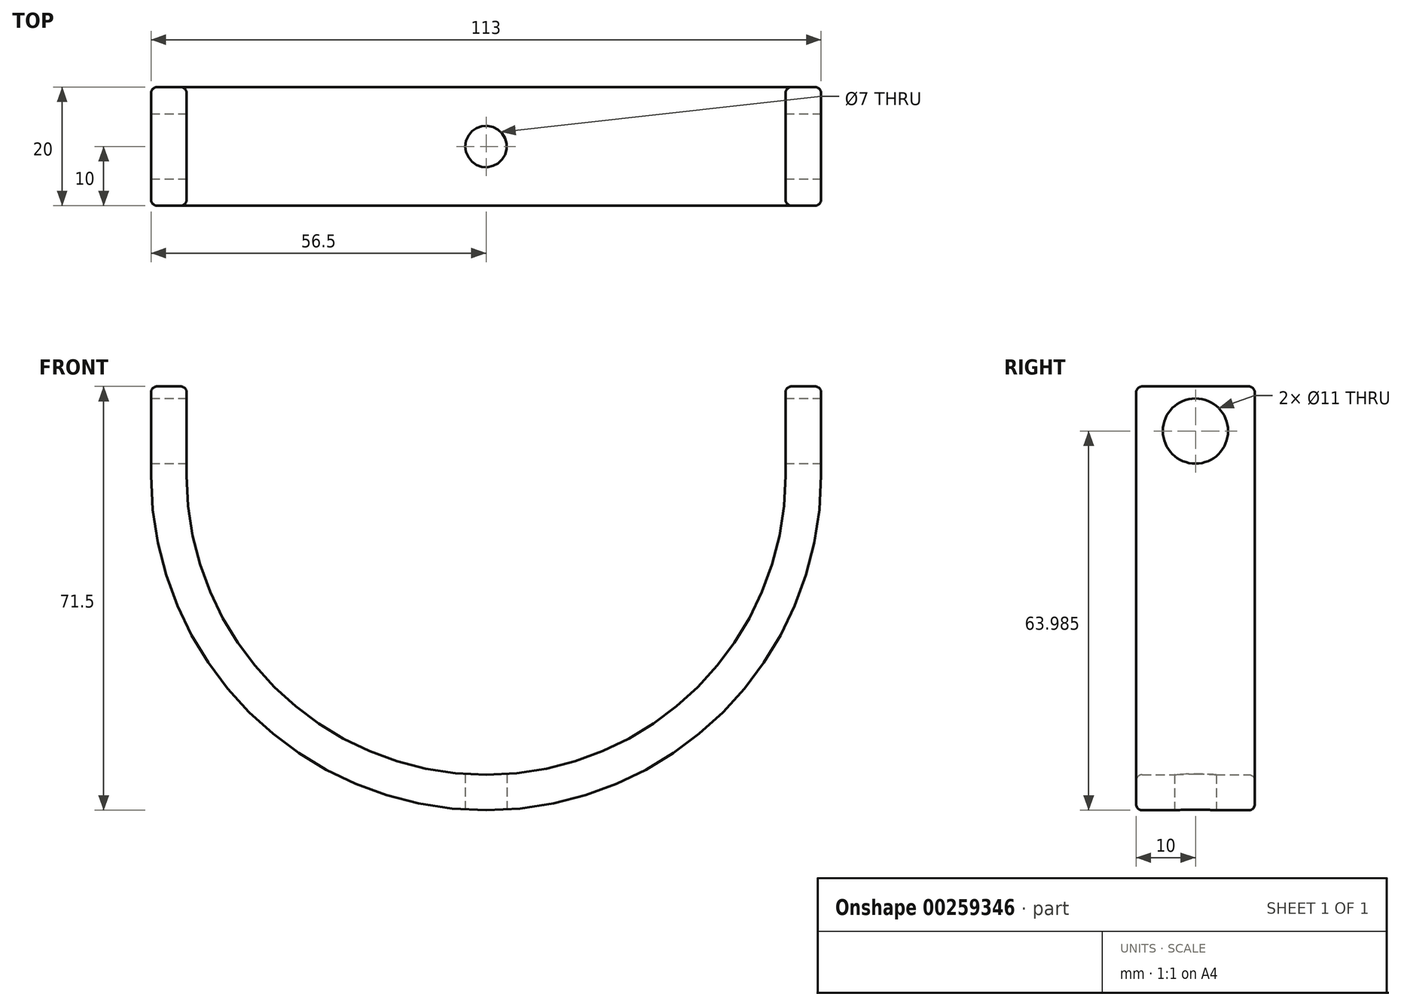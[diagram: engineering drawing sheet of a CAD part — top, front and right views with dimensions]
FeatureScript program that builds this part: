
annotation { "Feature Type Name" : "Feature", "Feature Type Description" : "" }
export const myFeature = defineFeature(function(context is Context, id is Id, definition is map)
    precondition{}
    {
        {
            var Q0;
            Q0=qCreatedBy(makeId("Front.planeOp"),FACE);
            var sketch = newSketch(context, id + "F0", { "sketchPlane" : qUnion([Q0])});
            skLineSegment(sketch, "E0", {"start": v(0, 0) * mm, "end": v(0, 68.85) * mm, "construction": true});
            skArc(sketch, "E1", {"start": v(-56.5, 50.5) * mm, "mid": v(0, -6) * mm, "end": v(56.5, 50.5) * mm});
            skLineSegment(sketch, "E2", {"start": v(56.5, 50.5) * mm, "end": v(56.5, 65.5) * mm});
            skLineSegment(sketch, "E3", {"start": v(56.5, 58) * mm, "end": v(30.23, 58) * mm, "construction": true});
            skLineSegment(sketch, "E4.MirrorCS", {"start": v(-56.5, 50.5) * mm, "end": v(-56.5, 65.5) * mm});
            skLineSegment(sketch, "E5.MirrorCS", {"start": v(-56.5, 58) * mm, "end": v(-30.23, 58) * mm, "construction": true});
            skLineSegment(sketch, "E6.MirrorCS", {"start": v(-56.5, 58) * mm, "end": v(-86.2, 58) * mm, "construction": true});
            skLineSegment(sketch, "E7.0", {"start": v(-50.5, 50.5) * mm, "end": v(-50.5, 65.5) * mm});
            skArc(sketch, "E7.1", {"start": v(-50.5, 50.5) * mm, "mid": v(0, 0) * mm, "end": v(50.5, 50.5) * mm});
            skLineSegment(sketch, "E7.2", {"start": v(50.5, 50.5) * mm, "end": v(50.5, 65.5) * mm});
            skLineSegment(sketch, "E8", {"start": v(-56.5, 65.5) * mm, "end": v(-50.5, 65.5) * mm});
            skLineSegment(sketch, "E9", {"start": v(50.5, 65.5) * mm, "end": v(56.5, 65.5) * mm});
            skSolve(sketch);
        }
        {
            var Q0;
            Q0=makeQuery(id+"F0.imprint","IMPRINT",FACE,{"disambiguationData":[TD([[makeQuery(id+"F0.imprint","IMPRINT",EDGE,{"derivedFrom":sQuery(id+"F0.wireOp",EDGE,"E1")}),1.0]])]});
            extrude(context, id + "F1", {"entities" : qUnion([Q0]), "endBound" : BoundingType.SYMMETRIC, "depth" : 20 * mm});
        }
        {
            var Q0;
            Q0=makeQuery(id+"F1.opExtrude","CAP_EDGE",EDGE,{"disambiguationData":[OSD([sQuery(id+"F0.wireOp",EDGE,"E7.1")])],"isStart":false});
            var Q1;
            Q1=makeQuery(id+"F1.opExtrude","CAP_EDGE",EDGE,{"disambiguationData":[OSD([sQuery(id+"F0.wireOp",EDGE,"E7.0")])],"isStart":false});
            var Q2;
            Q2=makeQuery(id+"F1.opExtrude","CAP_EDGE",EDGE,{"disambiguationData":[OSD([sQuery(id+"F0.wireOp",EDGE,"E7.2")])],"isStart":false});
            var Q3;
            Q3=makeQuery(id+"F1.opExtrude","CAP_EDGE",EDGE,{"disambiguationData":[OSD([sQuery(id+"F0.wireOp",EDGE,"E1")])],"isStart":false});
            var Q4;
            Q4=makeQuery(id+"F1.opExtrude","CAP_EDGE",EDGE,{"disambiguationData":[OSD([sQuery(id+"F0.wireOp",EDGE,"E4.MirrorCS")])],"isStart":false});
            var Q5;
            Q5=makeQuery(id+"F1.opExtrude","CAP_EDGE",EDGE,{"disambiguationData":[OSD([sQuery(id+"F0.wireOp",EDGE,"E7.0")])],"isStart":true});
            var Q6;
            Q6=makeQuery(id+"F1.opExtrude","CAP_EDGE",EDGE,{"disambiguationData":[OSD([sQuery(id+"F0.wireOp",EDGE,"E7.1")])],"isStart":true});
            var Q7;
            Q7=makeQuery(id+"F1.opExtrude","CAP_EDGE",EDGE,{"disambiguationData":[OSD([sQuery(id+"F0.wireOp",EDGE,"E7.2")])],"isStart":true});
            var Q8;
            Q8=makeQuery(id+"F1.opExtrude","CAP_EDGE",EDGE,{"disambiguationData":[OSD([sQuery(id+"F0.wireOp",EDGE,"E2")])],"isStart":true});
            var Q9;
            Q9=makeQuery(id+"F1.opExtrude","CAP_EDGE",EDGE,{"disambiguationData":[OSD([sQuery(id+"F0.wireOp",EDGE,"E1")])],"isStart":true});
            var Q10;
            Q10=makeQuery(id+"F1.opExtrude","CAP_EDGE",EDGE,{"disambiguationData":[OSD([sQuery(id+"F0.wireOp",EDGE,"E4.MirrorCS")])],"isStart":true});
            fillet(context, id + "F2", {"entities" : qUnion([Q0, Q1, Q2, Q3, Q4, Q5, Q6, Q7, Q8, Q9, Q10]), "radius" : 1 * mm, "tangentPropagation" : true, "allowEdgeOverflow" : false});
        }
        {
            var Q0;
            Q0=makeQuery(id+"F1.opExtrude","SWEPT_FACE",FACE,{"disambiguationData":[OSD([sQuery(id+"F0.wireOp",EDGE,"E2")])]});
            cPlane(context, id + "F3", {"entities" : qUnion([Q0]), "cplaneType" : CPlaneType.OFFSET, "offset" : 0 * mm, "width" : 150 * mm, "height" : 150 * mm});
        }
        {
            var Q0;
            Q0=qCreatedBy(id+"F3.planeOp",FACE);
            var sketch = newSketch(context, id + "F4", { "sketchPlane" : qUnion([Q0])});
            skCircle(sketch, "E10", {"center": v(0, 57.98) * mm, "radius": 4.55 * mm, "construction": true});
            skLineSegment(sketch, "E11", {"start": v(0, 57.98) * mm, "end": v(7.29, 57.71) * mm, "construction": true});
            skLineSegment(sketch, "E12", {"start": v(0, 57.98) * mm, "end": v(-3.28, 54.06) * mm, "construction": true});
            skCircle(sketch, "E13", {"center": v(0, 57.98) * mm, "radius": 5.5 * mm});
            skSolve(sketch);
        }
        {
            var Q0;
            Q0=makeQuery(id+"F4.imprint","IMPRINT",FACE,{"disambiguationData":[TD([[makeQuery(id+"F4.imprint","IMPRINT",EDGE,{"derivedFrom":sQuery(id+"F4.wireOp",EDGE,"E13")}),1.0]])]});
            extrude(context, id + "F5", {"entities" : qUnion([Q0]), "operationType" : NewBodyOperationType.REMOVE, "endBound" : BoundingType.THROUGH_ALL, "oppositeDirection" : true, "depth" : 25 * mm});
        }
        {
            var Q0;
            Q0=qCreatedBy(makeId("Top.planeOp"),FACE);
            cPlane(context, id + "F6", {"entities" : qUnion([Q0]), "cplaneType" : CPlaneType.OFFSET, "offset" : 25 * mm, "oppositeDirection" : true, "width" : 150 * mm, "height" : 150 * mm});
        }
        {
            var Q0;
            Q0=qCreatedBy(id+"F6.planeOp",FACE);
            var sketch = newSketch(context, id + "F7", { "sketchPlane" : qUnion([Q0])});
            skCircle(sketch, "E14", {"center": v(0, 0) * mm, "radius": 3.5 * mm});
            skSolve(sketch);
        }
        {
            var Q0;
            Q0 = qSketchRegion(id + "F7", true);
            extrude(context, id + "F8", {"entities" : qUnion([Q0]), "operationType" : NewBodyOperationType.REMOVE, "endBound" : BoundingType.THROUGH_ALL, "depth" : 60 * mm});
        }
        {
            var Q0;
            Q0=makeQuery(id+"F1.opExtrude","SWEPT_EDGE",EDGE,{"disambiguationData":[OSD([sQuery(id+"F0.wireOp",EDGE,"E7.0"),sQuery(id+"F0.wireOp",EDGE,"E8")])]});
            var Q1;
            Q1=makeQuery(id+"F2.opFillet","BLEND_EDGE",EDGE,{"blendedFrom":[makeQuery(id+"F1.opExtrude","CAP_EDGE",EDGE,{"disambiguationData":[OSD([sQuery(id+"F0.wireOp",EDGE,"E7.0")])],"isStart":false}),makeQuery(id+"F1.opExtrude","SWEPT_FACE",FACE,{"disambiguationData":[OSD([sQuery(id+"F0.wireOp",EDGE,"E8")])]})],"blendedInto":[makeQuery(id+"F1.opExtrude","SWEPT_FACE",FACE,{"disambiguationData":[OSD([sQuery(id+"F0.wireOp",EDGE,"E8")])]})]});
            var Q2;
            Q2=makeQuery(id+"F1.opExtrude","CAP_EDGE",EDGE,{"disambiguationData":[OSD([sQuery(id+"F0.wireOp",EDGE,"E8")])],"isStart":false});
            var Q3;
            Q3=makeQuery(id+"F1.opExtrude","SWEPT_EDGE",EDGE,{"disambiguationData":[OSD([sQuery(id+"F0.wireOp",EDGE,"E4.MirrorCS"),sQuery(id+"F0.wireOp",EDGE,"E8")])]});
            var Q4;
            Q4=makeQuery(id+"F2.opFillet","BLEND_EDGE",EDGE,{"blendedFrom":[makeQuery(id+"F1.opExtrude","CAP_EDGE",EDGE,{"disambiguationData":[OSD([sQuery(id+"F0.wireOp",EDGE,"E4.MirrorCS")])],"isStart":false}),makeQuery(id+"F1.opExtrude","SWEPT_FACE",FACE,{"disambiguationData":[OSD([sQuery(id+"F0.wireOp",EDGE,"E8")])]})],"blendedInto":[makeQuery(id+"F1.opExtrude","SWEPT_FACE",FACE,{"disambiguationData":[OSD([sQuery(id+"F0.wireOp",EDGE,"E8")])]})]});
            var Q5;
            Q5=makeQuery(id+"F2.opFillet","BLEND_EDGE",EDGE,{"blendedFrom":[makeQuery(id+"F1.opExtrude","CAP_EDGE",EDGE,{"disambiguationData":[OSD([sQuery(id+"F0.wireOp",EDGE,"E4.MirrorCS")])],"isStart":true}),makeQuery(id+"F1.opExtrude","SWEPT_FACE",FACE,{"disambiguationData":[OSD([sQuery(id+"F0.wireOp",EDGE,"E8")])]})],"blendedInto":[makeQuery(id+"F1.opExtrude","SWEPT_FACE",FACE,{"disambiguationData":[OSD([sQuery(id+"F0.wireOp",EDGE,"E8")])]})]});
            var Q6;
            Q6=makeQuery(id+"F1.opExtrude","CAP_EDGE",EDGE,{"disambiguationData":[OSD([sQuery(id+"F0.wireOp",EDGE,"E8")])],"isStart":true});
            var Q7;
            Q7=makeQuery(id+"F2.opFillet","BLEND_EDGE",EDGE,{"blendedFrom":[makeQuery(id+"F1.opExtrude","CAP_EDGE",EDGE,{"disambiguationData":[OSD([sQuery(id+"F0.wireOp",EDGE,"E7.0")])],"isStart":true}),makeQuery(id+"F1.opExtrude","SWEPT_FACE",FACE,{"disambiguationData":[OSD([sQuery(id+"F0.wireOp",EDGE,"E8")])]})],"blendedInto":[makeQuery(id+"F1.opExtrude","SWEPT_FACE",FACE,{"disambiguationData":[OSD([sQuery(id+"F0.wireOp",EDGE,"E8")])]})]});
            fillet(context, id + "F9", {"entities" : qUnion([Q0, Q1, Q2, Q3, Q4, Q5, Q6, Q7]), "radius" : 1 * mm, "tangentPropagation" : true, "allowEdgeOverflow" : false});
        }
        {
            var Q0;
            Q0=makeQuery(id+"F1.opExtrude","SWEPT_EDGE",EDGE,{"disambiguationData":[OSD([sQuery(id+"F0.wireOp",EDGE,"E2"),sQuery(id+"F0.wireOp",EDGE,"E9")])]});
            var Q1;
            Q1=makeQuery(id+"F2.opFillet","BLEND_EDGE",EDGE,{"blendedFrom":[makeQuery(id+"F1.opExtrude","CAP_EDGE",EDGE,{"disambiguationData":[OSD([sQuery(id+"F0.wireOp",EDGE,"E2")])],"isStart":false}),makeQuery(id+"F1.opExtrude","SWEPT_FACE",FACE,{"disambiguationData":[OSD([sQuery(id+"F0.wireOp",EDGE,"E9")])]})],"blendedInto":[makeQuery(id+"F1.opExtrude","SWEPT_FACE",FACE,{"disambiguationData":[OSD([sQuery(id+"F0.wireOp",EDGE,"E9")])]})]});
            var Q2;
            Q2=makeQuery(id+"F1.opExtrude","CAP_EDGE",EDGE,{"disambiguationData":[OSD([sQuery(id+"F0.wireOp",EDGE,"E9")])],"isStart":false});
            var Q3;
            Q3=makeQuery(id+"F2.opFillet","BLEND_EDGE",EDGE,{"blendedFrom":[makeQuery(id+"F1.opExtrude","CAP_EDGE",EDGE,{"disambiguationData":[OSD([sQuery(id+"F0.wireOp",EDGE,"E7.2")])],"isStart":false}),makeQuery(id+"F1.opExtrude","SWEPT_FACE",FACE,{"disambiguationData":[OSD([sQuery(id+"F0.wireOp",EDGE,"E9")])]})],"blendedInto":[makeQuery(id+"F1.opExtrude","SWEPT_FACE",FACE,{"disambiguationData":[OSD([sQuery(id+"F0.wireOp",EDGE,"E9")])]})]});
            var Q4;
            Q4=makeQuery(id+"F1.opExtrude","SWEPT_EDGE",EDGE,{"disambiguationData":[OSD([sQuery(id+"F0.wireOp",EDGE,"E7.2"),sQuery(id+"F0.wireOp",EDGE,"E9")])]});
            var Q5;
            Q5=makeQuery(id+"F2.opFillet","BLEND_EDGE",EDGE,{"blendedFrom":[makeQuery(id+"F1.opExtrude","CAP_EDGE",EDGE,{"disambiguationData":[OSD([sQuery(id+"F0.wireOp",EDGE,"E7.2")])],"isStart":true}),makeQuery(id+"F1.opExtrude","SWEPT_FACE",FACE,{"disambiguationData":[OSD([sQuery(id+"F0.wireOp",EDGE,"E9")])]})],"blendedInto":[makeQuery(id+"F1.opExtrude","SWEPT_FACE",FACE,{"disambiguationData":[OSD([sQuery(id+"F0.wireOp",EDGE,"E9")])]})]});
            var Q6;
            Q6=makeQuery(id+"F1.opExtrude","CAP_EDGE",EDGE,{"disambiguationData":[OSD([sQuery(id+"F0.wireOp",EDGE,"E9")])],"isStart":true});
            var Q7;
            Q7=makeQuery(id+"F2.opFillet","BLEND_EDGE",EDGE,{"blendedFrom":[makeQuery(id+"F1.opExtrude","CAP_EDGE",EDGE,{"disambiguationData":[OSD([sQuery(id+"F0.wireOp",EDGE,"E2")])],"isStart":true}),makeQuery(id+"F1.opExtrude","SWEPT_FACE",FACE,{"disambiguationData":[OSD([sQuery(id+"F0.wireOp",EDGE,"E9")])]})],"blendedInto":[makeQuery(id+"F1.opExtrude","SWEPT_FACE",FACE,{"disambiguationData":[OSD([sQuery(id+"F0.wireOp",EDGE,"E9")])]})]});
            fillet(context, id + "F10", {"entities" : qUnion([Q0, Q1, Q2, Q3, Q4, Q5, Q6, Q7]), "radius" : 1 * mm, "tangentPropagation" : true, "allowEdgeOverflow" : false});
        }
    });
